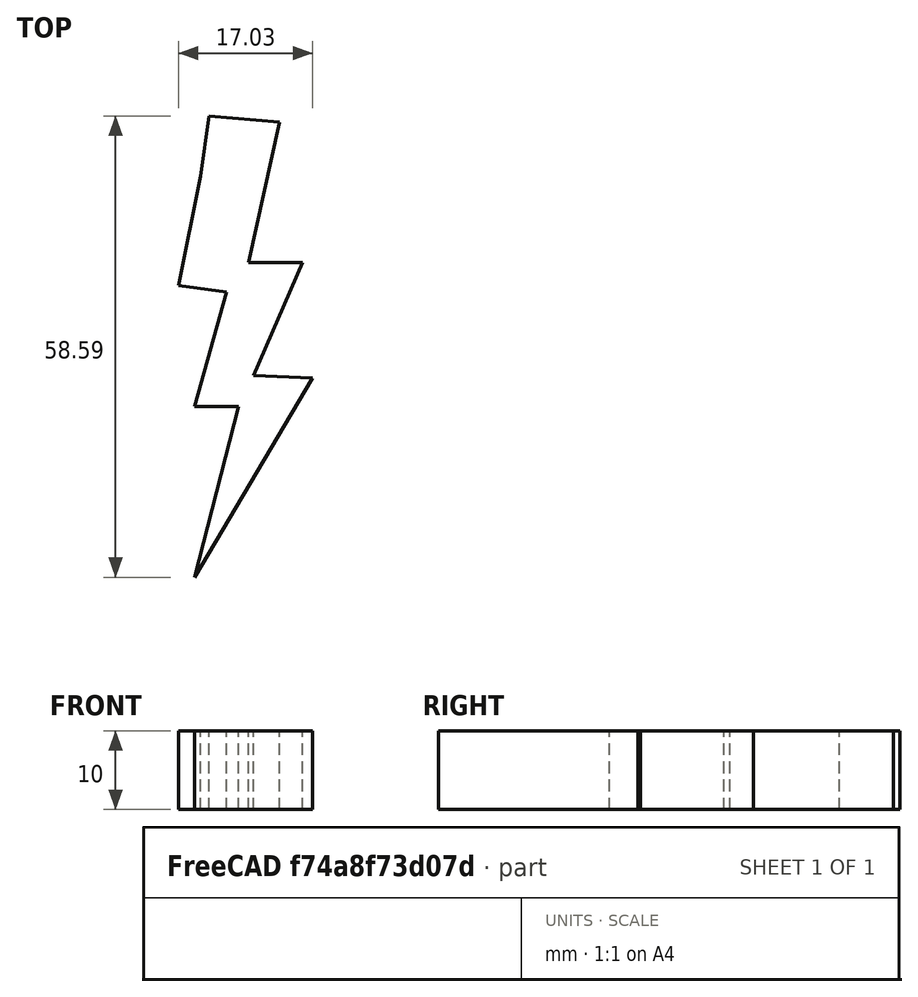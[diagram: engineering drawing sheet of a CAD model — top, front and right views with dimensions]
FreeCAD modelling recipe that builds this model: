
FCSTD DOCUMENT  (FreeCAD 0.20R29177 +426 (Git))
Label: Croquis1
License: All rights reserved
LicenseURL: http://en.wikipedia.org/wiki/All_rights_reserved
objects: Sketcher::SketchObject×2, PartDesign::Pad×1, PartDesign::Body×1
note: 5 computed .brp shape members not serialized (recipe doc carries the construction recipe); baked Part::Feature solids carry a one-line shape summary decoded from their .brp

FEATURE [Sketcher::SketchObject] Sketch
  FullyConstrained = false
  MapMode = 5
  Support = -> [XY_Plane]
  sketch-geometry (12):
    g0: LineSegment StartX=-7.1875 StartY=30.1562 StartZ=0 EndX=-9.99999 EndY=16.25 EndZ=0
    g1: LineSegment StartX=-9.99999 StartY=16.25 StartZ=0 EndX=-3.90625 EndY=15.4688 EndZ=0
    g2: LineSegment StartX=-3.90625 StartY=15.4688 StartZ=0 EndX=-7.96874 EndY=0.937498 EndZ=0
    g3: LineSegment StartX=-7.96874 StartY=0.937498 StartZ=0 EndX=-2.34375 EndY=0.937498 EndZ=0
    g4: LineSegment StartX=-2.34375 StartY=0.937498 StartZ=0 EndX=-7.96874 EndY=-20.7812 EndZ=0
    g5: LineSegment StartX=-7.96874 StartY=-20.7812 StartZ=0 EndX=7.03125 EndY=4.53125 EndZ=0
    g6: LineSegment StartX=7.03125 StartY=4.53125 StartZ=0 EndX=-0.468742 EndY=4.84375 EndZ=0
    g7: LineSegment StartX=-0.468742 StartY=4.84375 StartZ=0 EndX=5.78125 EndY=19.2187 EndZ=0
    g8: LineSegment StartX=5.78125 StartY=19.2187 StartZ=0 EndX=-1.09375 EndY=19.2187 EndZ=0
    g9: LineSegment StartX=-1.09375 StartY=19.2187 StartZ=0 EndX=2.8125 EndY=37.0312 EndZ=0
    g10: LineSegment StartX=2.8125 StartY=37.0312 StartZ=0 EndX=-6.09375 EndY=37.8125 EndZ=0
    g11: LineSegment StartX=-7.1875 StartY=30.1562 StartZ=0 EndX=-6.09375 EndY=37.8125 EndZ=0
  constraints (14):
    c: Coincident(g0,g1)
    c: Coincident(g1,g2)
    c: Coincident(g2,g3)
    c: Horizontal(g3)
    c: Coincident(g3,g4)
    c: Coincident(g4,g5)
    c: Coincident(g5,g6)
    c: Coincident(g6,g7)
    c: Coincident(g7,g8)
    c: Horizontal(g8)
    c: Coincident(g8,g9)
    c: Coincident(g9,g10)
    c: Coincident(g0,g11)
    c: Coincident(g11,g10)
FEATURE [Sketcher::SketchObject] Sketch001
  FullyConstrained = true
  MapMode = 5
  Support = -> [XY_Plane]
FEATURE [PartDesign::Pad] Pad
  Direction = (0,0,1)
  Length = 10
  Length2 = 10
  Profile = -> Sketch
  ReferenceAxis = -> Sketch [N_Axis]
  Type = 0
FEATURE [PartDesign::Body] Body
  Group = -> [Sketch,Sketch001,Pad]
  Origin = -> Origin
  Tip = -> Pad
